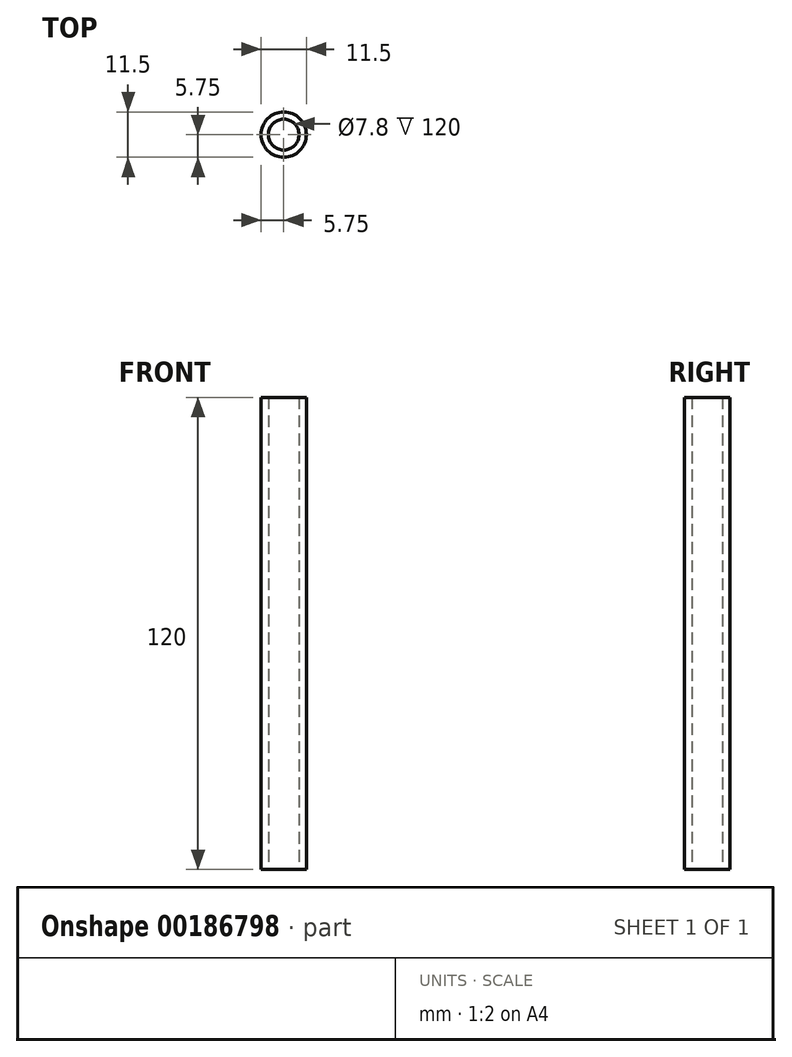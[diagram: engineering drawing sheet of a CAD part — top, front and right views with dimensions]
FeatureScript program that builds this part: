
annotation { "Feature Type Name" : "Feature", "Feature Type Description" : "" }
export const myFeature = defineFeature(function(context is Context, id is Id, definition is map)
    precondition{}
    {
        {
            var Q0;
            Q0=qCreatedBy(makeId("Top.planeOp"),FACE);
            var sketch = newSketch(context, id + "F0", { "sketchPlane" : qUnion([Q0])});
            skCircle(sketch, "E0", {"center": v(0, 0) * mm, "radius": 5.75 * mm});
            skCircle(sketch, "E1", {"center": v(0, 0) * mm, "radius": 3.9 * mm});
            skSolve(sketch);
        }
        {
            var Q0;
            Q0=makeQuery(id+"F0.imprint","IMPRINT",FACE,{"disambiguationData":[TD([[makeQuery(id+"F0.imprint","IMPRINT",EDGE,{"derivedFrom":sQuery(id+"F0.wireOp",EDGE,"YLP8zI7w-ljKk-E7Sk-Arkr-PSR9LZ2Rsa6R.bottom")}),-1.0]])]});
            var Q1;
            Q1=makeQuery(id+"F0.imprint","IMPRINT",FACE,{"disambiguationData":[TD([[makeQuery(id+"F0.imprint","IMPRINT",EDGE,{"derivedFrom":sQuery(id+"F0.wireOp",EDGE,"E0")}),1.0]])]});
            extrude(context, id + "F1", {"entities" : qUnion([Q0, Q1]), "depth" : 120 * mm});
        }
    });
